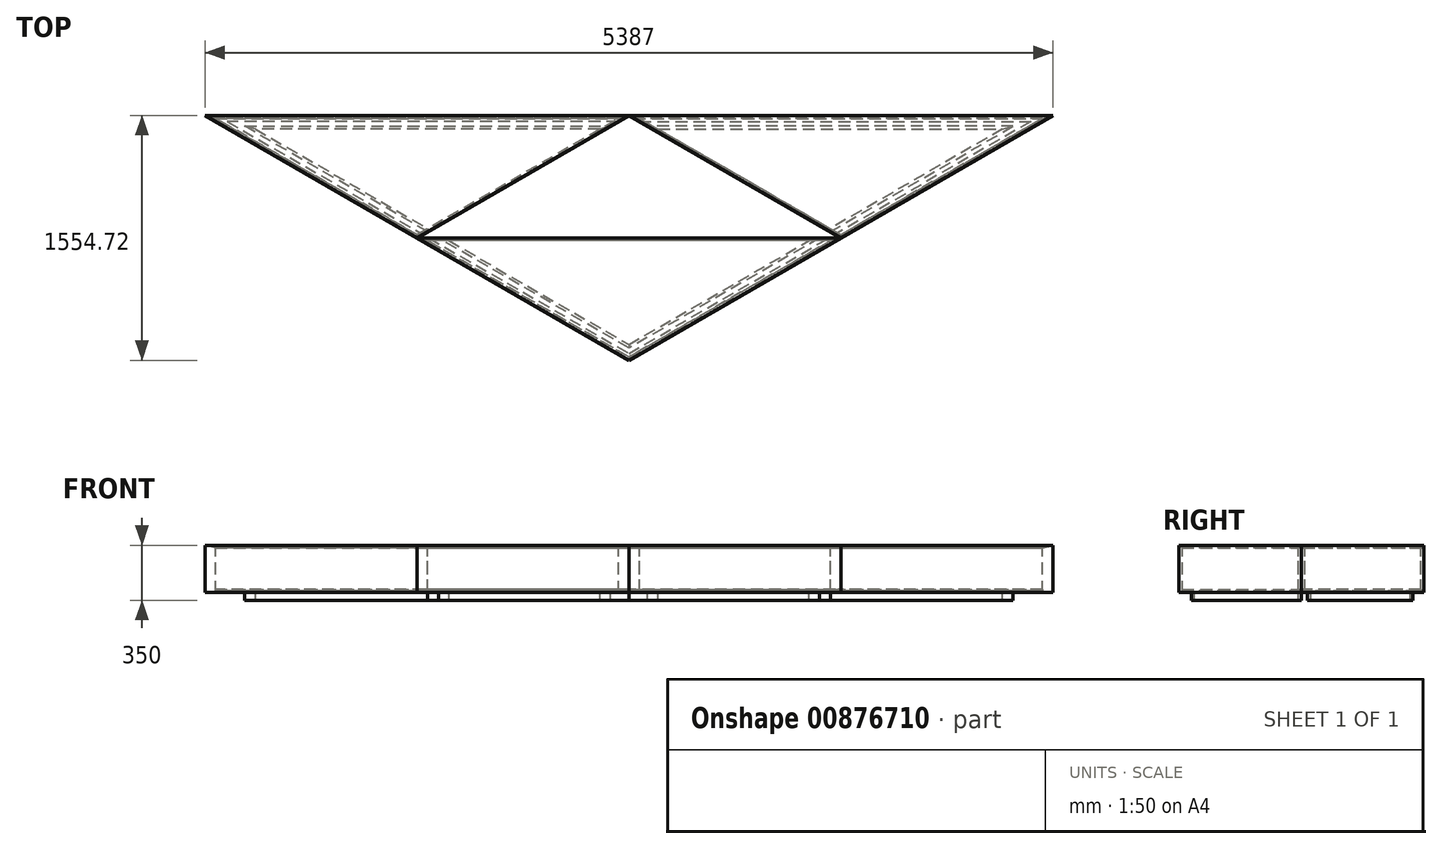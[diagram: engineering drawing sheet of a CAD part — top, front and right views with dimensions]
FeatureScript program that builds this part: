
annotation { "Feature Type Name" : "Feature", "Feature Type Description" : "" }
export const myFeature = defineFeature(function(context is Context, id is Id, definition is map)
    precondition{}
    {
        {
            var Q0;
            Q0=qCreatedBy(makeId("Top.planeOp"),FACE);
            var sketch = newSketch(context, id + "F0", { "sketchPlane" : qUnion([Q0])});
            skLineSegment(sketch, "E0", {"start": v(-2644.8, 1440.91) * mm, "end": v(48.7, 1440.91) * mm});
            skLineSegment(sketch, "E1", {"start": v(48.7, 1440.91) * mm, "end": v(2742.2, 1440.91) * mm});
            skLineSegment(sketch, "E2", {"start": v(2742.2, 1440.91) * mm, "end": v(1395.46, 663.55) * mm});
            skLineSegment(sketch, "E3", {"start": v(1395.46, 663.55) * mm, "end": v(48.7, -113.8) * mm});
            skLineSegment(sketch, "E4", {"start": v(48.7, -113.8) * mm, "end": v(-1298.04, 663.55) * mm});
            skLineSegment(sketch, "E5", {"start": v(-1298.04, 663.55) * mm, "end": v(-2644.8, 1440.91) * mm});
            skLineSegment(sketch, "E6", {"start": v(-1298.04, 663.55) * mm, "end": v(48.7, 1440.91) * mm});
            skLineSegment(sketch, "E7", {"start": v(1395.46, 663.55) * mm, "end": v(48.7, 1440.91) * mm});
            skLineSegment(sketch, "E8", {"start": v(-1298.04, 663.55) * mm, "end": v(1395.46, 663.55) * mm});
            skSolve(sketch);
        }
        {
            var Q0;
            Q0=makeQuery(id+"F0.imprint","IMPRINT",FACE,{"disambiguationData":[TD([[makeQuery(id+"F0.imprint","IMPRINT",EDGE,{"derivedFrom":sQuery(id+"F0.wireOp",EDGE,"E0")}),-1.0]])]});
            var Q1;
            Q1=makeQuery(id+"F0.imprint","IMPRINT",FACE,{"disambiguationData":[TD([[makeQuery(id+"F0.imprint","IMPRINT",EDGE,{"derivedFrom":sQuery(id+"F0.wireOp",EDGE,"E3")}),-1.0]])]});
            var Q2;
            Q2=makeQuery(id+"F0.imprint","IMPRINT",FACE,{"disambiguationData":[TD([[makeQuery(id+"F0.imprint","IMPRINT",EDGE,{"derivedFrom":sQuery(id+"F0.wireOp",EDGE,"E1")}),-1.0]])]});
            extrude(context, id + "F1", {"entities" : qUnion([Q0, Q1, Q2]), "depth" : 18 * mm, "offsetDistance" : 25 * mm});
        }
        {
            var Q0;
            Q0=makeQuery(id+"F0.imprint","IMPRINT",FACE,{"disambiguationData":[TD([[makeQuery(id+"F0.imprint","IMPRINT",EDGE,{"derivedFrom":sQuery(id+"F0.wireOp",EDGE,"E6")}),-1.0]])]});
            extrude(context, id + "F2", {"entities" : qUnion([Q0]), "depth" : 18 * mm, "offsetDistance" : 25 * mm});
        }
        {
            var Q0;
            Q0=makeQuery(id+"F1.opExtrude","CAP_EDGE",EDGE,{"disambiguationData":[OSD([sQuery(id+"F0.wireOp",EDGE,"E5")])],"isStart":true});
            var Q1;
            Q1=makeQuery(id+"F1.opExtrude","CAP_EDGE",EDGE,{"disambiguationData":[OSD([sQuery(id+"F0.wireOp",EDGE,"E4")])],"isStart":true});
            var Q2;
            Q2=makeQuery(id+"F1.opExtrude","CAP_EDGE",EDGE,{"disambiguationData":[OSD([sQuery(id+"F0.wireOp",EDGE,"E3")])],"isStart":true});
            var Q3;
            Q3=makeQuery(id+"F1.opExtrude","CAP_EDGE",EDGE,{"disambiguationData":[OSD([sQuery(id+"F0.wireOp",EDGE,"E2")])],"isStart":true});
            var Q4;
            Q4=makeQuery(id+"F1.opExtrude","CAP_EDGE",EDGE,{"disambiguationData":[OSD([sQuery(id+"F0.wireOp",EDGE,"E0")])],"isStart":true});
            var Q5;
            Q5=makeQuery(id+"F1.opExtrude","CAP_EDGE",EDGE,{"disambiguationData":[OSD([sQuery(id+"F0.wireOp",EDGE,"E1")])],"isStart":true});
            chamfer(context, id + "F3", {"entities" : qUnion([Q0, Q1, Q2, Q3, Q4, Q5]), "width" : 18 * mm, "tangentPropagation" : true});
        }
        {
            var Q0;
            Q0=qCreatedBy(makeId("Top.planeOp"),FACE);
            var sketch = newSketch(context, id + "F4", { "sketchPlane" : qUnion([Q0])});
            skLineSegment(sketch, "E9.0", {"start": v(48.7, -113.8) * mm, "end": v(-1298.04, 663.55) * mm});
            skLineSegment(sketch, "E10.0", {"start": v(-1298.04, 663.55) * mm, "end": v(-2644.8, 1440.91) * mm});
            skLineSegment(sketch, "E11.0", {"start": v(-2644.8, 1440.91) * mm, "end": v(48.7, 1440.91) * mm});
            skLineSegment(sketch, "E12.0", {"start": v(48.7, 1440.91) * mm, "end": v(2742.2, 1440.91) * mm});
            skLineSegment(sketch, "E13.0", {"start": v(2742.2, 1440.91) * mm, "end": v(1395.46, 663.55) * mm});
            skLineSegment(sketch, "E14.0", {"start": v(1395.46, 663.55) * mm, "end": v(48.7, -113.8) * mm});
            skLineSegment(sketch, "E15", {"start": v(48.7, 1440.91) * mm, "end": v(1395.46, 663.55) * mm});
            skLineSegment(sketch, "E16", {"start": v(1395.46, 663.55) * mm, "end": v(-1298.04, 663.55) * mm});
            skLineSegment(sketch, "E17", {"start": v(-1298.04, 663.55) * mm, "end": v(48.7, 1440.91) * mm});
            skLineSegment(sketch, "E18.0", {"start": v(115.9, 1422.91) * mm, "end": v(2675.02, 1422.91) * mm});
            skLineSegment(sketch, "E18.1", {"start": v(115.9, 1422.91) * mm, "end": v(1395.46, 684.33) * mm});
            skLineSegment(sketch, "E18.2", {"start": v(2675.02, 1422.91) * mm, "end": v(1395.46, 684.33) * mm});
            skLineSegment(sketch, "E19", {"start": v(2742.2, 1440.91) * mm, "end": v(2675.02, 1422.91) * mm});
            skLineSegment(sketch, "E20", {"start": v(48.7, 1440.91) * mm, "end": v(115.9, 1422.91) * mm});
            skLineSegment(sketch, "E21", {"start": v(1395.46, 684.33) * mm, "end": v(1395.46, 663.55) * mm});
            skLineSegment(sketch, "E22.0", {"start": v(-2577.6, 1422.91) * mm, "end": v(-18.48, 1422.91) * mm});
            skLineSegment(sketch, "E22.1", {"start": v(-1298.04, 684.33) * mm, "end": v(-2577.6, 1422.91) * mm});
            skLineSegment(sketch, "E22.2", {"start": v(-1298.04, 684.33) * mm, "end": v(-18.48, 1422.91) * mm});
            skLineSegment(sketch, "E23.0", {"start": v(1328.27, 645.55) * mm, "end": v(-1230.85, 645.55) * mm});
            skLineSegment(sketch, "E23.1", {"start": v(1328.27, 645.55) * mm, "end": v(48.7, -93.03) * mm});
            skLineSegment(sketch, "E23.2", {"start": v(48.7, -93.03) * mm, "end": v(-1230.85, 645.55) * mm});
            skLineSegment(sketch, "E24", {"start": v(-2644.8, 1440.91) * mm, "end": v(-2577.6, 1422.91) * mm});
            skLineSegment(sketch, "E25", {"start": v(-18.48, 1422.91) * mm, "end": v(48.7, 1440.91) * mm});
            skLineSegment(sketch, "E26", {"start": v(-1298.04, 684.33) * mm, "end": v(-1298.04, 663.55) * mm});
            skLineSegment(sketch, "E27", {"start": v(-1298.04, 663.55) * mm, "end": v(-1230.85, 645.55) * mm});
            skLineSegment(sketch, "E28", {"start": v(1328.27, 645.55) * mm, "end": v(1395.46, 663.55) * mm});
            skLineSegment(sketch, "E29", {"start": v(48.7, -93.03) * mm, "end": v(48.7, -113.8) * mm});
            skSolve(sketch);
        }
        {
            var Q0;
            Q0=makeQuery(id+"F4.imprint","IMPRINT",FACE,{"disambiguationData":[TD([[makeQuery(id+"F4.imprint","IMPRINT",EDGE,{"derivedFrom":sQuery(id+"F4.wireOp",EDGE,"E10.0")}),-1.0]])]});
            var Q1;
            Q1=makeQuery(id+"F4.imprint","IMPRINT",FACE,{"disambiguationData":[TD([[makeQuery(id+"F4.imprint","IMPRINT",EDGE,{"derivedFrom":sQuery(id+"F4.wireOp",EDGE,"E16")}),1.0]])]});
            var Q2;
            Q2=makeQuery(id+"F4.imprint","IMPRINT",FACE,{"disambiguationData":[TD([[makeQuery(id+"F4.imprint","IMPRINT",EDGE,{"derivedFrom":sQuery(id+"F4.wireOp",EDGE,"E13.0")}),-1.0]])]});
            extrude(context, id + "F5", {"entities" : qUnion([Q0, Q1, Q2]), "oppositeDirection" : true, "depth" : 282 * mm, "offsetDistance" : 25 * mm, "hasSecondDirection" : true, "secondDirectionOppositeDirection" : false, "secondDirectionDepth" : 18 * mm});
        }
        {
            var Q0;
            Q0=makeQuery(id+"F4.imprint","IMPRINT",FACE,{"disambiguationData":[TD([[makeQuery(id+"F4.imprint","IMPRINT",EDGE,{"derivedFrom":sQuery(id+"F4.wireOp",EDGE,"E11.0")}),-1.0]])]});
            var Q1;
            Q1=makeQuery(id+"F4.imprint","IMPRINT",FACE,{"disambiguationData":[TD([[makeQuery(id+"F4.imprint","IMPRINT",EDGE,{"derivedFrom":sQuery(id+"F4.wireOp",EDGE,"E15")}),1.0]])]});
            var Q2;
            Q2=makeQuery(id+"F4.imprint","IMPRINT",FACE,{"disambiguationData":[TD([[makeQuery(id+"F4.imprint","IMPRINT",EDGE,{"derivedFrom":sQuery(id+"F4.wireOp",EDGE,"E14.0")}),-1.0]])]});
            extrude(context, id + "F6", {"entities" : qUnion([Q0, Q1, Q2]), "oppositeDirection" : true, "depth" : 282 * mm, "offsetDistance" : 25 * mm, "hasSecondDirection" : true, "secondDirectionOppositeDirection" : false, "secondDirectionDepth" : 18 * mm});
        }
        {
            var Q0;
            Q0=makeQuery(id+"F4.imprint","IMPRINT",FACE,{"disambiguationData":[TD([[makeQuery(id+"F4.imprint","IMPRINT",EDGE,{"derivedFrom":sQuery(id+"F4.wireOp",EDGE,"E17")}),1.0]])]});
            var Q1;
            Q1=makeQuery(id+"F4.imprint","IMPRINT",FACE,{"disambiguationData":[TD([[makeQuery(id+"F4.imprint","IMPRINT",EDGE,{"derivedFrom":sQuery(id+"F4.wireOp",EDGE,"E9.0")}),-1.0]])]});
            var Q2;
            Q2=makeQuery(id+"F4.imprint","IMPRINT",FACE,{"disambiguationData":[TD([[makeQuery(id+"F4.imprint","IMPRINT",EDGE,{"derivedFrom":sQuery(id+"F4.wireOp",EDGE,"E12.0")}),-1.0]])]});
            extrude(context, id + "F7", {"entities" : qUnion([Q0, Q1, Q2]), "oppositeDirection" : true, "depth" : 282 * mm, "offsetDistance" : 25 * mm, "hasSecondDirection" : true, "secondDirectionOppositeDirection" : false, "secondDirectionDepth" : 18 * mm});
        }
        {
            var Q0;
            Q0=makeQuery(id+"F5.opExtrude","CAP_EDGE",EDGE,{"disambiguationData":[OSD([sQuery(id+"F4.wireOp",EDGE,"E22.1")])],"isStart":true});
            var Q1;
            Q1=makeQuery(id+"F7.opExtrude","CAP_EDGE",EDGE,{"disambiguationData":[OSD([sQuery(id+"F4.wireOp",EDGE,"E22.2")])],"isStart":true});
            var Q2;
            Q2=makeQuery(id+"F5.opExtrude","CAP_EDGE",EDGE,{"disambiguationData":[OSD([sQuery(id+"F4.wireOp",EDGE,"E23.0")])],"isStart":true});
            var Q3;
            Q3=makeQuery(id+"F7.opExtrude","CAP_EDGE",EDGE,{"disambiguationData":[OSD([sQuery(id+"F4.wireOp",EDGE,"E23.2")])],"isStart":true});
            var Q4;
            Q4=makeQuery(id+"F6.opExtrude","CAP_EDGE",EDGE,{"disambiguationData":[OSD([sQuery(id+"F4.wireOp",EDGE,"E22.0")])],"isStart":true});
            var Q5;
            Q5=makeQuery(id+"F6.opExtrude","CAP_EDGE",EDGE,{"disambiguationData":[OSD([sQuery(id+"F4.wireOp",EDGE,"E18.1")])],"isStart":true});
            var Q6;
            Q6=makeQuery(id+"F7.opExtrude","CAP_EDGE",EDGE,{"disambiguationData":[OSD([sQuery(id+"F4.wireOp",EDGE,"E18.0")])],"isStart":true});
            var Q7;
            Q7=makeQuery(id+"F5.opExtrude","CAP_EDGE",EDGE,{"disambiguationData":[OSD([sQuery(id+"F4.wireOp",EDGE,"E18.2")])],"isStart":true});
            var Q8;
            Q8=makeQuery(id+"F6.opExtrude","CAP_EDGE",EDGE,{"disambiguationData":[OSD([sQuery(id+"F4.wireOp",EDGE,"E23.1")])],"isStart":true});
            chamfer(context, id + "F8", {"entities" : qUnion([Q0, Q1, Q2, Q3, Q4, Q5, Q6, Q7, Q8]), "width" : 18 * mm, "tangentPropagation" : true});
        }
        {
            var Q0;
            Q0=makeQuery(id+"F7.opExtrude","CAP_FACE",FACE,{"disambiguationData":[OSD([sQuery(id+"F4.wireOp",EDGE,"E12.0"),sQuery(id+"F4.wireOp",EDGE,"E18.0"),sQuery(id+"F4.wireOp",EDGE,"E19"),sQuery(id+"F4.wireOp",EDGE,"E20")])],"isStart":false});
            var sketch = newSketch(context, id + "F9", { "sketchPlane" : qUnion([Q0])});
            skLineSegment(sketch, "E30.0", {"start": v(83.62, -1422.91) * mm, "end": v(2675.02, -1422.91) * mm});
            skLineSegment(sketch, "E31.0", {"start": v(2675.02, -1422.91) * mm, "end": v(1377.95, -674.23) * mm});
            skLineSegment(sketch, "E32.0", {"start": v(83.12, -1421.05) * mm, "end": v(1376.95, -674.23) * mm});
            skPoint(sketch, "E33.newPointA", {"position": v(115.9, -1422.91) * mm});
            skPoint(sketch, "E33.newPointB", {"position": v(48.7, -1440.91) * mm});
            skArc(sketch, "E33.filletArc", {"start": v(83.12, -1421.05) * mm, "mid": v(82.66, -1422.17) * mm, "end": v(83.62, -1422.91) * mm});
            skPoint(sketch, "E34.newPointA", {"position": v(1395.46, -684.33) * mm});
            skPoint(sketch, "E34.newPointB", {"position": v(1395.46, -663.55) * mm});
            skArc(sketch, "E34.filletArc", {"start": v(1377.95, -674.23) * mm, "mid": v(1377.45, -674.1) * mm, "end": v(1376.95, -674.23) * mm});
            skSolve(sketch);
        }
        {
            var Q0;
            Q0 = qSketchRegion(id + "F9", true);
            extrude(context, id + "F10", {"entities" : qUnion([Q0]), "oppositeDirection" : true, "depth" : 18 * mm, "offsetDistance" : 25 * mm});
        }
        {
            var Q0;
            Q0=makeQuery(id+"F6.opExtrude","CAP_VERTEX",VERTEX,{"disambiguationData":[OSD([sQuery(id+"F4.wireOp",EDGE,"E9.0"),sQuery(id+"F4.wireOp",EDGE,"E14.0"),sQuery(id+"F4.wireOp",EDGE,"E29")])],"isStart":false});
            var Q1;
            Q1=sQuery(id+"F4.wireOp",VERTEX,"E9.0.start");
            var Q2;
            {var subQ0=sQuery(id+"F4.wireOp",EDGE,"E11.0");var subQ1=sQuery(id+"F4.wireOp",EDGE,"E25");Q2=makeQuery(id+"F6.opExtrude","CAP_VERTEX",VERTEX,{"disambiguationData":[OSD([subQ0,sQuery(id+"F4.wireOp",EDGE,"E12.0"),sQuery(id+"F4.wireOp",EDGE,"E15"),sQuery(id+"F4.wireOp",EDGE,"E17"),sQuery(id+"F4.wireOp",EDGE,"E20"),subQ1]),topologyDisambiguationEdgeConnected([makeQuery(id+"F4.imprint","IMPRINT",EDGE,{"derivedFrom":subQ0})])],"isStart":false});}
            cPlane(context, id + "F11", {"entities" : qUnion([Q0, Q1, Q2]), "cplaneType" : CPlaneType.THREE_POINT, "offset" : 25 * mm, "width" : 150 * mm, "height" : 150 * mm});
        }
        {
            var Q0;
            Q0=makeQuery(id+"F7.opExtrude","CAP_FACE",FACE,{"disambiguationData":[OSD([sQuery(id+"F4.wireOp",EDGE,"E9.0"),sQuery(id+"F4.wireOp",EDGE,"E23.2"),sQuery(id+"F4.wireOp",EDGE,"E27"),sQuery(id+"F4.wireOp",EDGE,"E29")])],"isStart":false});
            var sketch = newSketch(context, id + "F12", { "sketchPlane" : qUnion([Q0])});
            skLineSegment(sketch, "E35", {"start": v(48.7, 93.03) * mm, "end": v(1359.45, -663.55) * mm});
            skLineSegment(sketch, "E36", {"start": v(1359.45, -663.55) * mm, "end": v(-1262.04, -663.55) * mm});
            skLineSegment(sketch, "E37", {"start": v(48.7, 93.03) * mm, "end": v(-1262.04, -663.55) * mm});
            skSolve(sketch);
        }
        {
            var Q0;
            Q0 = qSketchRegion(id + "F12", true);
            extrude(context, id + "F13", {"entities" : qUnion([Q0]), "oppositeDirection" : true, "depth" : 18 * mm, "offsetDistance" : 25 * mm});
        }
        {
            var Q0;
            Q0=makeQuery(id+"F10.opExtrude","CAP_FACE",FACE,{"disambiguationData":[OSD([sQuery(id+"F9.wireOp",EDGE,"E30.0"),sQuery(id+"F9.wireOp",EDGE,"E31.0"),sQuery(id+"F9.wireOp",EDGE,"E32.0"),sQuery(id+"F9.wireOp",EDGE,"E33.filletArc"),sQuery(id+"F9.wireOp",EDGE,"E34.filletArc")])],"isStart":true});
            var sketch = newSketch(context, id + "F14", { "sketchPlane" : qUnion([Q0])});
            skLineSegment(sketch, "E38.0", {"start": v(2600.36, -1402.91) * mm, "end": v(1357.45, -685.49) * mm});
            skLineSegment(sketch, "E38.1", {"start": v(114.54, -1402.91) * mm, "end": v(2600.36, -1402.91) * mm});
            skLineSegment(sketch, "E39", {"start": v(1377.45, -673.94) * mm, "end": v(2675.02, -1422.91) * mm});
            skLineSegment(sketch, "E40", {"start": v(2675.02, -1422.91) * mm, "end": v(79.9, -1422.91) * mm});
            skLineSegment(sketch, "E41", {"start": v(79.9, -1422.91) * mm, "end": v(114.54, -1402.91) * mm});
            skLineSegment(sketch, "E42", {"start": v(1357.45, -685.49) * mm, "end": v(1377.45, -673.94) * mm});
            skSolve(sketch);
        }
        {
            var Q0;
            Q0 = qSketchRegion(id + "F14", true);
            extrude(context, id + "F15", {"entities" : qUnion([Q0]), "operationType" : NewBodyOperationType.REMOVE, "oppositeDirection" : true, "depth" : 9 * mm, "offsetDistance" : 25 * mm});
        }
        {
            var Q0;
            Q0=makeQuery(id+"F10.opExtrude","SWEPT_BODY",BODY,{"disambiguationData":[OSD([sQuery(id+"F9.wireOp",EDGE,"E30.0"),sQuery(id+"F9.wireOp",EDGE,"E31.0"),sQuery(id+"F9.wireOp",EDGE,"E32.0"),sQuery(id+"F9.wireOp",EDGE,"E33.filletArc"),sQuery(id+"F9.wireOp",EDGE,"E34.filletArc")])]});
            var Q1;
            Q1=qCreatedBy(id+"F11.planeOp",FACE);
            mirror(context, id + "F16", {"entities" : qUnion([Q0]), "mirrorPlane" : qUnion([Q1])});
        }
        {
            var Q0;
            Q0=makeQuery(id+"F13.opExtrude","CAP_FACE",FACE,{"disambiguationData":[OSD([sQuery(id+"F12.wireOp",EDGE,"E35"),sQuery(id+"F12.wireOp",EDGE,"E36"),sQuery(id+"F12.wireOp",EDGE,"E37")])],"isStart":true});
            var sketch = newSketch(context, id + "F17", { "sketchPlane" : qUnion([Q0])});
            skLineSegment(sketch, "E43", {"start": v(1359.45, -663.55) * mm, "end": v(48.7, 93.03) * mm});
            skLineSegment(sketch, "E44", {"start": v(48.7, 93.03) * mm, "end": v(-1262.04, -663.55) * mm});
            skLineSegment(sketch, "E45", {"start": v(-1262.04, -663.55) * mm, "end": v(-1222.03, -663.55) * mm});
            skLineSegment(sketch, "E46", {"start": v(-1222.03, -663.55) * mm, "end": v(48.7, 69.93) * mm});
            skLineSegment(sketch, "E47", {"start": v(48.7, 69.93) * mm, "end": v(1319.44, -663.55) * mm});
            skLineSegment(sketch, "E48", {"start": v(1319.44, -663.55) * mm, "end": v(1359.45, -663.55) * mm});
            skSolve(sketch);
        }
        {
            var Q0;
            Q0 = qSketchRegion(id + "F17", true);
            extrude(context, id + "F18", {"entities" : qUnion([Q0]), "operationType" : NewBodyOperationType.REMOVE, "oppositeDirection" : true, "depth" : 9 * mm, "offsetDistance" : 25 * mm});
        }
        {
            var Q0;
            Q0=makeQuery(id+"F16.opPattern","COPY",FACE,{"derivedFrom":makeQuery(id+"F10.opExtrude","CAP_FACE",FACE,{"disambiguationData":[OSD([sQuery(id+"F9.wireOp",EDGE,"E30.0"),sQuery(id+"F9.wireOp",EDGE,"E31.0"),sQuery(id+"F9.wireOp",EDGE,"E32.0"),sQuery(id+"F9.wireOp",EDGE,"E33.filletArc"),sQuery(id+"F9.wireOp",EDGE,"E34.filletArc")])],"isStart":true}),"instanceName":"1"});
            var sketch = newSketch(context, id + "F19", { "sketchPlane" : qUnion([Q0])});
            skLineSegment(sketch, "E49", {"start": v(-2390.96, -1372.91) * mm, "end": v(-69.1, -1372.91) * mm});
            skLineSegment(sketch, "E50", {"start": v(-1230.03, -702.8) * mm, "end": v(-2390.96, -1372.91) * mm});
            skLineSegment(sketch, "E51", {"start": v(-136.3, -1354.91) * mm, "end": v(-2323.77, -1354.91) * mm});
            skLineSegment(sketch, "E52", {"start": v(-2323.77, -1354.91) * mm, "end": v(-1230.03, -723.6) * mm});
            skLineSegment(sketch, "E53", {"start": v(-69.1, -1372.91) * mm, "end": v(-136.3, -1354.91) * mm});
            skLineSegment(sketch, "E54", {"start": v(-1230.03, -723.6) * mm, "end": v(-1230.03, -702.8) * mm});
            skLineSegment(sketch, "E55", {"start": v(-2323.77, -1354.91) * mm, "end": v(-2390.96, -1372.91) * mm});
            skLineSegment(sketch, "E56", {"start": v(-1386.87, -1372.91) * mm, "end": v(-1386.87, -1354.91) * mm, "construction": true});
            skLineSegment(sketch, "E57", {"start": v(-1241.27, -717.1) * mm, "end": v(-1232.27, -701.52) * mm, "construction": true});
            skLineSegment(sketch, "E58", {"start": v(-1457.9, -855.12) * mm, "end": v(-1466.9, -839.53) * mm, "construction": true});
            skLineSegment(sketch, "E59", {"start": v(1259.43, -663.55) * mm, "end": v(48.7, 35.3) * mm});
            skLineSegment(sketch, "E60", {"start": v(48.7, 35.3) * mm, "end": v(-1162.02, -663.55) * mm});
            skLineSegment(sketch, "E61", {"start": v(-1162.02, -663.55) * mm, "end": v(1259.43, -663.55) * mm});
            skLineSegment(sketch, "E62", {"start": v(1192.24, -645.55) * mm, "end": v(-1094.83, -645.55) * mm});
            skLineSegment(sketch, "E63", {"start": v(-1094.83, -645.55) * mm, "end": v(48.7, 14.51) * mm});
            skLineSegment(sketch, "E64", {"start": v(48.7, 14.51) * mm, "end": v(1192.24, -645.55) * mm});
            skLineSegment(sketch, "E65", {"start": v(1259.43, -663.55) * mm, "end": v(1192.24, -645.55) * mm});
            skLineSegment(sketch, "E66", {"start": v(48.7, 14.51) * mm, "end": v(48.7, 35.3) * mm});
            skLineSegment(sketch, "E67", {"start": v(-1162.02, -663.55) * mm, "end": v(-1094.83, -645.55) * mm});
            skLineSegment(sketch, "E68", {"start": v(48.7, -663.55) * mm, "end": v(48.7, -645.55) * mm, "construction": true});
            skLineSegment(sketch, "E69", {"start": v(-523.06, -315.52) * mm, "end": v(-532.06, -299.93) * mm, "construction": true});
            skLineSegment(sketch, "E70", {"start": v(620.47, -315.52) * mm, "end": v(629.47, -299.93) * mm, "construction": true});
            skSolve(sketch);
        }
        {
            var Q0;
            Q0=makeQuery(id+"F19.imprint","IMPRINT",FACE,{"disambiguationData":[TD([[makeQuery(id+"F19.imprint","IMPRINT",EDGE,{"derivedFrom":sQuery(id+"F19.wireOp",EDGE,"E49")}),1.0]])]});
            var Q1;
            Q1=makeQuery(id+"F19.imprint","IMPRINT",FACE,{"disambiguationData":[TD([[makeQuery(id+"F19.imprint","IMPRINT",EDGE,{"derivedFrom":sQuery(id+"F19.wireOp",EDGE,"E60")}),1.0]])]});
            extrude(context, id + "F20", {"entities" : qUnion([Q0, Q1]), "depth" : 50 * mm, "offsetDistance" : 25 * mm});
        }
        {
            var Q0;
            Q0=makeQuery(id+"F19.imprint","IMPRINT",FACE,{"disambiguationData":[TD([[makeQuery(id+"F19.imprint","IMPRINT",EDGE,{"derivedFrom":sQuery(id+"F19.wireOp",EDGE,"E50")}),1.0]])]});
            var Q1;
            Q1=makeQuery(id+"F19.imprint","IMPRINT",FACE,{"disambiguationData":[TD([[makeQuery(id+"F19.imprint","IMPRINT",EDGE,{"derivedFrom":sQuery(id+"F19.wireOp",EDGE,"E59")}),1.0]])]});
            extrude(context, id + "F21", {"entities" : qUnion([Q0, Q1]), "depth" : 50 * mm, "offsetDistance" : 25 * mm});
        }
        {
            var Q0;
            Q0=makeQuery(id+"F19.imprint","IMPRINT",FACE,{"disambiguationData":[TD([[makeQuery(id+"F19.imprint","IMPRINT",EDGE,{"derivedFrom":sQuery(id+"F19.wireOp",EDGE,"E61")}),1.0]])]});
            var Q1;
            Q1=makeQuery(id+"F19.imprint","IMPRINT",FACE,{"disambiguationData":[TD([[makeQuery(id+"F19.imprint","IMPRINT",EDGE,{"derivedFrom":sQuery(id+"F19.wireOp",EDGE,"NU6TsBFG-ud3D-KsgD-if7x-VBO0ghh2Sadm")}),1.0]])]});
            extrude(context, id + "F22", {"entities" : qUnion([Q0, Q1]), "depth" : 50 * mm, "offsetDistance" : 25 * mm});
        }
        {
            var Q0;
            Q0=makeQuery(id+"F20.opExtrude","SWEPT_BODY",BODY,{"disambiguationData":[OSD([sQuery(id+"F19.wireOp",EDGE,"E49"),sQuery(id+"F19.wireOp",EDGE,"E51"),sQuery(id+"F19.wireOp",EDGE,"E53"),sQuery(id+"F19.wireOp",EDGE,"E55")])]});
            var Q1;
            Q1=makeQuery(id+"F22.opExtrude","SWEPT_BODY",BODY,{"disambiguationData":[OSD([sQuery(id+"F19.wireOp",EDGE,"NU6TsBFG-ud3D-KsgD-if7x-VBO0ghh2Sadm"),sQuery(id+"F19.wireOp",EDGE,"0q0McGBa-xHK0-1bSa-F8DR-mYRG5XO4jdlI"),sQuery(id+"F19.wireOp",EDGE,"E53"),sQuery(id+"F19.wireOp",EDGE,"E54")])]});
            var Q2;
            Q2=makeQuery(id+"F21.opExtrude","SWEPT_BODY",BODY,{"disambiguationData":[OSD([sQuery(id+"F19.wireOp",EDGE,"E50"),sQuery(id+"F19.wireOp",EDGE,"E52"),sQuery(id+"F19.wireOp",EDGE,"E54"),sQuery(id+"F19.wireOp",EDGE,"E55")])]});
            var Q3;
            Q3=qCreatedBy(id+"F11.planeOp",FACE);
            mirror(context, id + "F23", {"entities" : qUnion([Q0, Q1, Q2]), "mirrorPlane" : qUnion([Q3])});
        }
    });
